# Revit family: Cumberland-Alia_Metal-Lounge1
name_source: partatom
category: Furniture
revit_build: Autodesk Revit 2014 (Build: 20130308_1515(x64)
units: mm (PartAtom-declared; Revit-internal decimal feet)

## types (6) — shared parameters
Arm Finish = CUM - Linen - Beige
Assembly Code = E2020200
Back Finish = CUM - Linen - Beige
Depth = 32"
Height = 29"
Keynote = 12500
Leg Finish = CUM - METAL
Low Emitting Finish = Yes
Low Emitting Material = Yes
Manufacturer = Cumberland
Salvage or Reuse = Yes
Seat Finish = CUM - Linen - Beige
Type Comments = Alia Lounge
URL = www.cumberlandfurniture.com
zero-valued in all types: Percentage of Recycled Content

## per-type parameters (varying)
| type | # Seat | Arm #1 | Arm #2 | Description | Dist Arm | Panel Finish | Seat Dist | Width |
| 2633 | 2 | Yes | No | Fully Upholstered Surround, 31"w x 29"h x 32"d" | 31" | CUM - Maple - Wood | 22 3/16" | 31" |
| 2634 | 2 | Yes | No | Fully Upholstered Surround, 58"w x 29"h x 32"d" | 58" | <By Category> | 24 19/32" | 58" |
| 2635 | 3 | Yes | No | Fully Upholstered Surround, 82"w x 29"h x 32"d" | 82" | <By Category> | 24 5/16" | 82" |
| 2630 | 2 | No | Yes | Wood Surround, 31"w x 29"h x 32"d" | 31" | CUM - Maple - Wood | 22 3/16" | 31" |
| 2631 | 2 | No | Yes | Wood Surround, 58"w x 29"h x 32"d" | 58" | CUM - Maple - Wood | 24 19/32" | 58" |
| 2632 | 3 | No | Yes | Wood Surround, 82"w x 29"h x 32"d" | 82" | CUM - Maple - Wood | 24 5/16" | 82" |

note: column(s) folded — value = type name in every type: Model

## geometry (parser evidence)
native form markers: Sweep x6
no freeform markers — native parametric forms only
